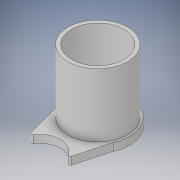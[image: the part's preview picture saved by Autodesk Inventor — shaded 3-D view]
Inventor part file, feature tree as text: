
AUTODESK INVENTOR PART (.ipt)
format: ipt  version: 2018.3 (Build 223284000, 284)  size: 153,088 bytes
history: native  units: in
note: dims shown in document units (in); Inventor stores cm internally (conversion verified against a paired STEP export)
features: extrude x5, plane x2, sketch x1
ambient origin geometry x8: Origin, YZ Plane, XZ Plane, XY Plane, X Axis, Y Axis, Z Axis, Center Point
bodies: Solid1 (feature_tree)
feature tree (8):
  sketch  "Sketch1"  dims[d11=0.3386in d12=30.0deg d13=0.436in d17=0.0375in d18=0.0375in d19=0.375in d20=0.091in d21=0.0in d22=0.581in d23=0.5625in d24=0.0in d25=0.83in d26=0.0in d28=0.0in d29=0.8281in d30=0.0in d31=-0.58in d33=0.8281in d34=0.0in]
  extrude  "Extrusion1"  TaperAngle=30.0deg  [1 undecoded]
  extrude  "Extrusion2"  Depth=0.83in
  extrude  "Extrusion3"  Depth=0.83in
  plane  "Work Plane1"
  extrude  "Extrusion4"  Depth=0.375in
  plane  "Work Plane2"
  extrude  "Extrusion5"  Depth=0.091in TaperAngle=0.0deg
note: 1 required parameter value undecoded (feature->parameter linkage not recoverable at this tier; creation-order binding heuristic only, values carry confidence <= 0.55)
